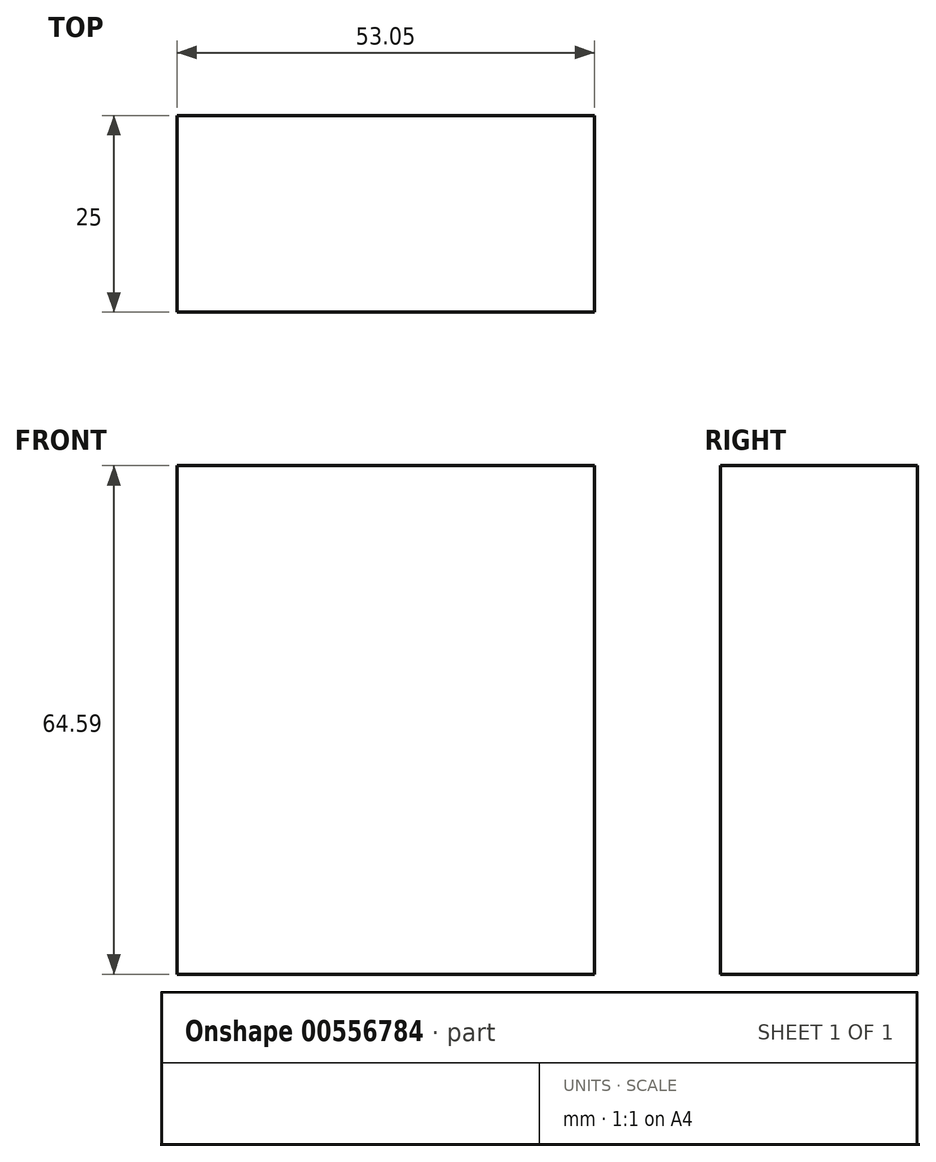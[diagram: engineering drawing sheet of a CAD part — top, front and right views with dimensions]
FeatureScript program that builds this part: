
annotation { "Feature Type Name" : "Feature", "Feature Type Description" : "" }
export const myFeature = defineFeature(function(context is Context, id is Id, definition is map)
    precondition{}
    {
        {
            var Q0;
            Q0=qCreatedBy(makeId("Front.planeOp"),FACE);
            var sketch = newSketch(context, id + "F0", { "sketchPlane" : qUnion([Q0])});
            skLineSegment(sketch, "E0.bottom", {"start": v(-53.05, 41.27) * mm, "end": v(0, 41.27) * mm});
            skLineSegment(sketch, "E0.top", {"start": v(-53.05, -23.32) * mm, "end": v(0, -23.32) * mm});
            skLineSegment(sketch, "E0.left", {"start": v(-53.05, 41.27) * mm, "end": v(-53.05, -23.32) * mm});
            skLineSegment(sketch, "E0.right", {"start": v(0, 41.27) * mm, "end": v(0, -23.32) * mm});
            skSolve(sketch);
        }
        {
            var Q0;
            Q0=makeQuery(id+"F0.imprint","IMPRINT",FACE,{"disambiguationData":[TD([[makeQuery(id+"F0.imprint","IMPRINT",EDGE,{"derivedFrom":sQuery(id+"F0.wireOp",EDGE,"E0.bottom")}),-1.0]])]});
            var Q1;
            Q1 = qSketchRegion(id + "F0", true);
            extrude(context, id + "F1", {"entities" : qUnion([Q0, Q1]), "depth" : 25 * mm, "offsetDistance" : 25 * mm});
        }
    });
